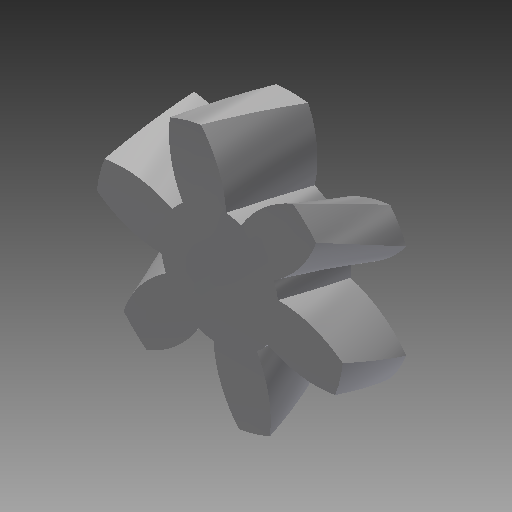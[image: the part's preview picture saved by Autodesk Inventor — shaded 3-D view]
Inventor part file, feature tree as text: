
AUTODESK INVENTOR PART (.ipt)
format: ipt  version: 2017 SP1 (Build 210196100, 196)  size: 229,888 bytes
history: native  units: mm (DEFAULTED — no unit token found)
features: plane x3, other x3, sketch x2, extrude x1
ambient origin geometry x8: Origin, YZ Plane, XZ Plane, XY Plane, X Axis, Y Axis, Z Axis, Center Point
bodies: Solid1 (feature_tree)
feature tree (9):
  extrude  "Extrusion1"  Depth=10.0mm TaperAngle=0.0deg
  plane  "Work Plane2"
  plane  "Work Plane8"
  plane  "Work Plane9"
  other  "Engrenage cylindrique"
  sketch  "Sketch1"  dims[d0=34.188431mm d1=10.0mm d2=0.0mm]
  sketch  "Sketch2"  dims[d3=26.24881mm d4=10.0mm d5=0.0mm d16=26.24881mm d17=0.0mm d34=30.0deg d39=0.0mm d41=0.0mm d43=26.24881mm d46=26.24881mm d47=0.0mm d48=0.0mm]
  other  "Srf1"
  other  "Diamètre primitif"
